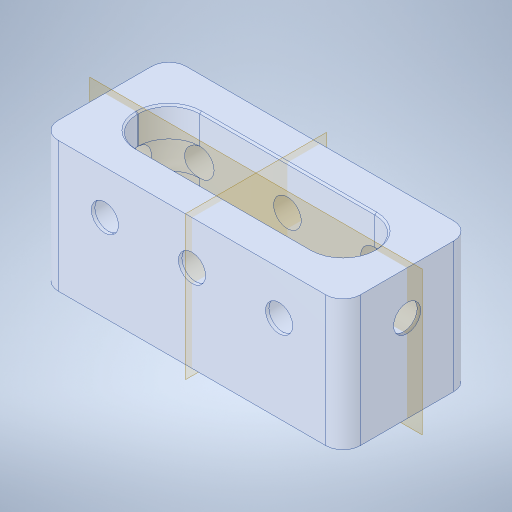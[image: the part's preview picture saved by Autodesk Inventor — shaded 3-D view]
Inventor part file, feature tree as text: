
AUTODESK INVENTOR PART (.ipt)
format: ipt  version: 2023.4 (Build 274418000, 418)  size: 471,040 bytes
history: native  units: in
note: dims shown in document units (in); Inventor stores cm internally (conversion verified against a paired STEP export)
features: sketch x5, hole x3, projected_geometry x3, extrude x2, chamfer x1
ambient origin geometry x8: Origin, YZ Plane, XZ Plane, XY Plane, X Axis, Y Axis, Z Axis, Center Point
bodies: Solid1 (feature_tree)
feature tree (14):
  extrude  "Extrusion1"  Depth=1.0in TaperAngle=0.0deg
  hole  "Hole1"  [1 undecoded]
  hole  "Hole2"  [1 undecoded]
  hole  "Hole3"  [1 undecoded]
  extrude  "Extrusion2"  [1 undecoded]
  sketch  "Sketch1"  dims[d0=0.0625in d1=1.0in d2=0.0in]
  projected_geometry  "Projected Loop1"
  sketch  "Sketch2"  dims[d3=0.156in d4=0.38in d5=0.385in d6=0.25in d7=0.563in d8=1.0in d9=0.8108in]
  projected_geometry  "Projected Loop2"
  sketch  "Sketch3"  dims[d10=0.196in d11=0.5in d12=0.375in d13=0.25in d14=0.5635in d15=1.0in d16=0.8108in]
  sketch  "Sketch4"  dims[d17=0.156in d18=0.38in d19=0.385in d20=0.25in d21=0.563in d22=1.0in d23=0.8108in d24=0.0625in]
  sketch  "Sketch5"  dims[d25=1.0in d26=0.0in]
  projected_geometry  "Projected Loop3"
  chamfer  "Chamfer2"  [1 undecoded]
note: 5 required parameter values undecoded (feature->parameter linkage not recoverable at this tier; creation-order binding heuristic only, values carry confidence <= 0.55)
